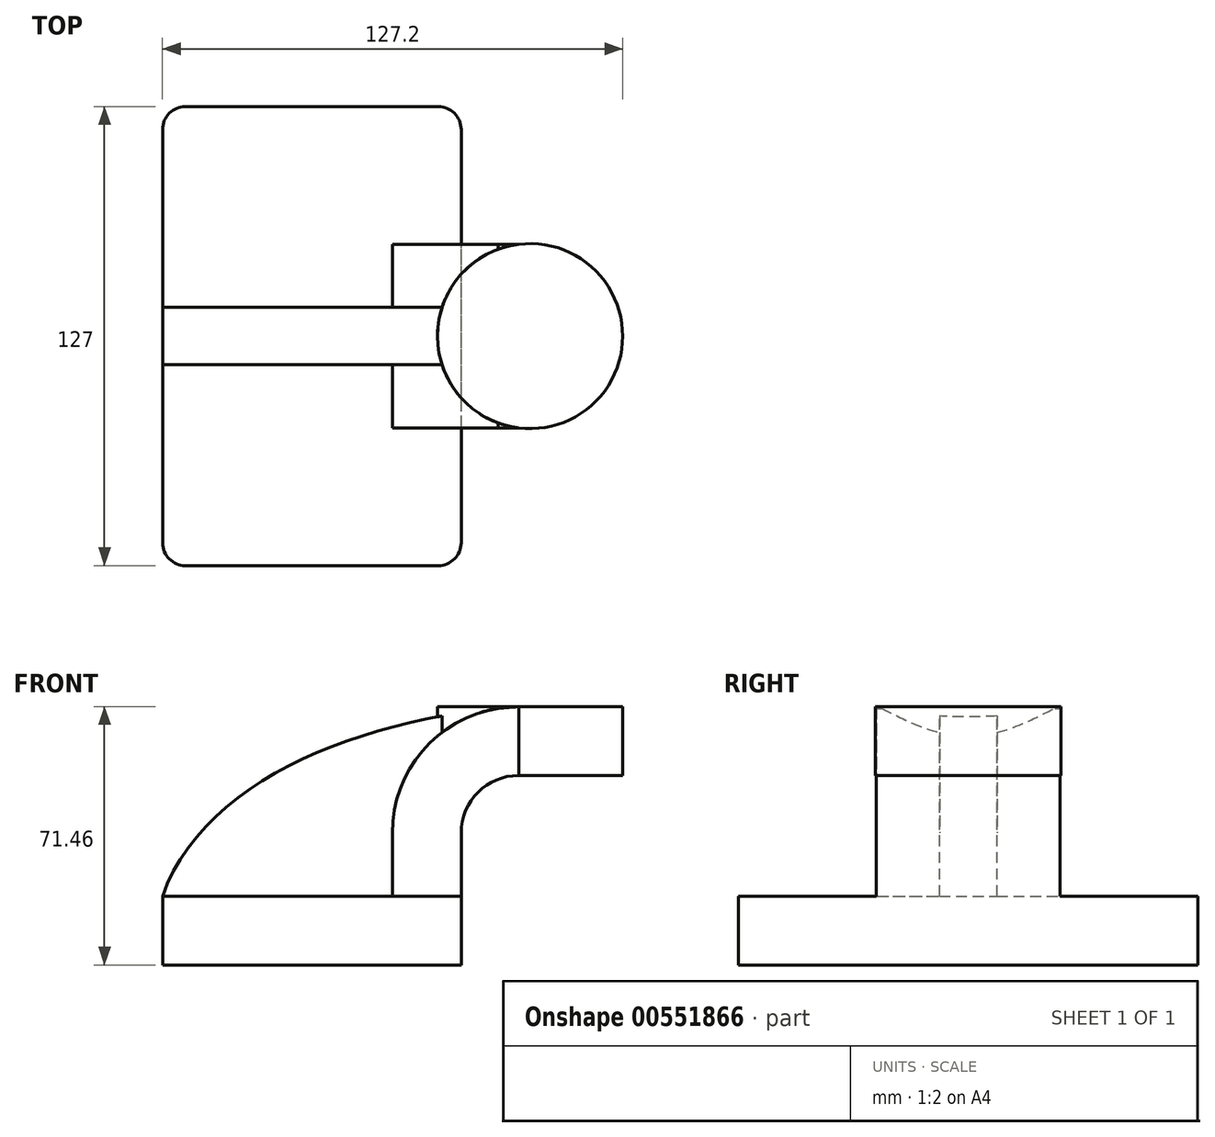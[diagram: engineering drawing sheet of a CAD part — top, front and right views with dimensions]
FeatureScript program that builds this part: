
annotation { "Feature Type Name" : "Feature", "Feature Type Description" : "" }
export const myFeature = defineFeature(function(context is Context, id is Id, definition is map)
    precondition{}
    {
        {
            var Q0;
            Q0=qCreatedBy(makeId("Front.planeOp"),FACE);
            var sketch = newSketch(context, id + "F0", { "sketchPlane" : qUnion([Q0])});
            skLineSegment(sketch, "E0.bottom", {"start": v(-41.28, 9.52) * mm, "end": v(41.27, 9.53) * mm});
            skLineSegment(sketch, "E0.top", {"start": v(-41.28, -9.53) * mm, "end": v(41.28, -9.53) * mm});
            skLineSegment(sketch, "E0.left", {"start": v(-41.28, 9.52) * mm, "end": v(-41.27, -9.53) * mm});
            skLineSegment(sketch, "E0.right", {"start": v(41.28, 9.53) * mm, "end": v(41.28, -9.52) * mm});
            skPoint(sketch, "E0.middle", {"position": v(0, 0) * mm});
            skLineSegment(sketch, "E1.bottom", {"start": v(60.32, 38.1) * mm, "end": v(111.12, 38.1) * mm});
            skLineSegment(sketch, "E1.top", {"start": v(60.32, 66.68) * mm, "end": v(111.12, 66.68) * mm});
            skLineSegment(sketch, "E1.left", {"start": v(60.32, 38.1) * mm, "end": v(60.32, 66.68) * mm});
            skLineSegment(sketch, "E1.right", {"start": v(111.12, 38.1) * mm, "end": v(111.12, 66.68) * mm});
            skPoint(sketch, "E1.middle", {"position": v(85.72, 52.39) * mm});
            skLineSegment(sketch, "E2", {"start": v(41.27, 9.53) * mm, "end": v(41.27, 27) * mm});
            skArc(sketch, "E3", {"start": v(41.27, 27) * mm, "mid": v(45.92, 38.23) * mm, "end": v(57.15, 42.88) * mm});
            skLineSegment(sketch, "E4", {"start": v(57.15, 42.88) * mm, "end": v(85.92, 42.88) * mm});
            skLineSegment(sketch, "E5.0", {"start": v(57.15, 61.93) * mm, "end": v(85.92, 61.93) * mm});
            skArc(sketch, "E5.1", {"start": v(22.23, 27) * mm, "mid": v(32.45, 51.7) * mm, "end": v(57.15, 61.93) * mm});
            skLineSegment(sketch, "E5.2", {"start": v(22.22, 9.53) * mm, "end": v(22.22, 27) * mm});
            skLineSegment(sketch, "E6", {"start": v(85.92, 38.1) * mm, "end": v(85.92, 66.68) * mm});
            skPoint(sketch, "E6.endSnap0", {"position": v(85.72, 66.68) * mm});
            skFitSpline(sketch, "E7", {"points": [v(-41.28, 9.52) * mm, v(57.15, 61.93) * mm], "startDerivative": vector(34.99, 99.13) * mm, "endDerivative": vector(124.18, 8.2) * mm});
            skSolve(sketch);
        }
        {
            var Q0;
            Q0=makeQuery(id+"F0.imprint","IMPRINT",FACE,{"disambiguationData":[TD([[makeQuery(id+"F0.imprint","IMPRINT",EDGE,{"derivedFrom":sQuery(id+"F0.wireOp",EDGE,"E0.top")}),1.0]])]});
            extrude(context, id + "F1", {"entities" : qUnion([Q0]), "endBound" : BoundingType.SYMMETRIC, "depth" : 127 * mm, "offsetDistance" : 25.4 * mm});
        }
        {
            var Q0;
            {var subQ1=sQuery(id+"F0.wireOp",EDGE,"E2");Q0=makeQuery(id+"F0.imprint","IMPRINT",FACE,{"disambiguationData":[TD([[makeQuery(id+"F0.imprint","IMPRINT",EDGE,{"derivedFrom":subQ1}),1.0]])]});}
            extrude(context, id + "F2", {"entities" : qUnion([Q0]), "operationType" : NewBodyOperationType.ADD, "endBound" : BoundingType.SYMMETRIC, "depth" : 50.8 * mm, "offsetDistance" : 25.4 * mm});
        }
        {
            var Q0;
            {var subQ3=sQuery(id+"F0.wireOp",EDGE,"E5.2");Q0=makeQuery(id+"F0.imprint","IMPRINT",FACE,{"disambiguationData":[TD([[makeQuery(id+"F0.imprint","IMPRINT",EDGE,{"derivedFrom":subQ3}),1.0]])]});}
            extrude(context, id + "F3", {"entities" : qUnion([Q0]), "operationType" : NewBodyOperationType.ADD, "endBound" : BoundingType.SYMMETRIC, "depth" : 15.88 * mm, "offsetDistance" : 25.4 * mm});
        }
        {
            var Q0;
            {var subQ0=sQuery(id+"F0.wireOp",EDGE,"E4");var subQ1=sQuery(id+"F0.wireOp",EDGE,"E1.left");var subQ2=makeQuery(id+"F0.imprint","INTERSECT",VERTEX,{"derivedFrom":[subQ1,subQ0]});Q0=makeQuery(id+"F0.imprint","IMPRINT",FACE,{"disambiguationData":[TD([[makeQuery(id+"F0.imprint","IMPRINT",EDGE,{"disambiguationData":[TD([[subQ2,-1.0]])],"derivedFrom":subQ1}),-1.0]])]});}
            var Q1;
            Q1=sQuery(id+"F0.wireOp",EDGE,"E1.left");
            revolve(context, id + "F4", {"operationType" : NewBodyOperationType.ADD, "entities" : qUnion([Q0]), "axis" : qUnion([Q1]), "revolveType" : RevolveType.FULL});
        }
        {
            var Q0;
            Q0=makeQuery(id+"F1.opExtrude","CAP_EDGE",EDGE,{"disambiguationData":[OSD([sQuery(id+"F0.wireOp",EDGE,"E0.right")])],"isStart":false});
            var Q1;
            Q1=makeQuery(id+"F1.opExtrude","CAP_EDGE",EDGE,{"disambiguationData":[OSD([sQuery(id+"F0.wireOp",EDGE,"E0.left")])],"isStart":false});
            var Q2;
            Q2=makeQuery(id+"F1.opExtrude","CAP_EDGE",EDGE,{"disambiguationData":[OSD([sQuery(id+"F0.wireOp",EDGE,"E0.left")])],"isStart":true});
            var Q3;
            Q3=makeQuery(id+"F1.opExtrude","CAP_EDGE",EDGE,{"disambiguationData":[OSD([sQuery(id+"F0.wireOp",EDGE,"E0.right")])],"isStart":true});
            fillet(context, id + "F5", {"entities" : qUnion([Q0, Q1, Q2, Q3]), "radius" : 6.35 * mm, "tangentPropagation" : true, "allowEdgeOverflow" : false});
        }
    });
